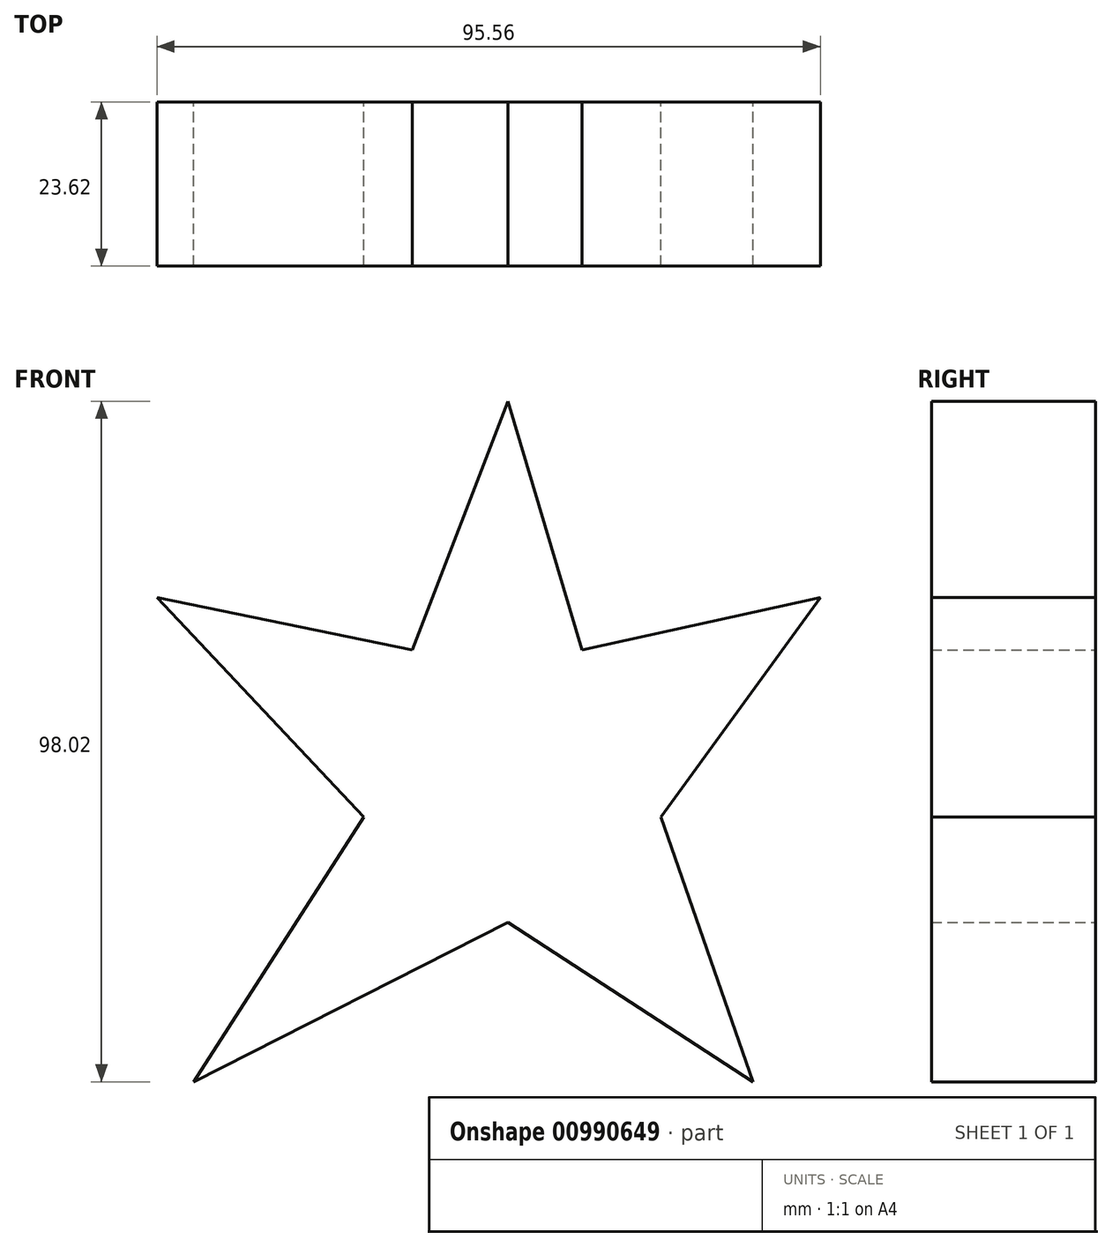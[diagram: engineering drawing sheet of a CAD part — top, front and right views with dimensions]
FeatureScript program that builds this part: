
annotation { "Feature Type Name" : "Feature", "Feature Type Description" : "" }
export const myFeature = defineFeature(function(context is Context, id is Id, definition is map)
    precondition{}
    {
        {
            var Q0;
            Q0=qCreatedBy(makeId("Front.planeOp"),FACE);
            var sketch = newSketch(context, id + "F0", { "sketchPlane" : qUnion([Q0])});
            skLineSegment(sketch, "E0", {"start": v(0, 53.18) * mm, "end": v(-13.75, 17.35) * mm});
            skLineSegment(sketch, "E1", {"start": v(-13.75, 17.35) * mm, "end": v(-50.53, 24.93) * mm});
            skLineSegment(sketch, "E2", {"start": v(-50.53, 24.93) * mm, "end": v(-20.76, -6.73) * mm});
            skLineSegment(sketch, "E3", {"start": v(-20.76, -6.73) * mm, "end": v(-45.22, -44.84) * mm});
            skLineSegment(sketch, "E4", {"start": v(-45.22, -44.84) * mm, "end": v(0, -21.9) * mm});
            skLineSegment(sketch, "E5", {"start": v(0, -21.9) * mm, "end": v(35.36, -44.84) * mm});
            skLineSegment(sketch, "E6", {"start": v(35.36, -44.84) * mm, "end": v(22.09, -6.73) * mm});
            skLineSegment(sketch, "E7", {"start": v(22.09, -6.73) * mm, "end": v(45.03, 24.93) * mm});
            skLineSegment(sketch, "E8", {"start": v(45.03, 24.93) * mm, "end": v(10.71, 17.35) * mm});
            skLineSegment(sketch, "E9", {"start": v(10.71, 17.35) * mm, "end": v(0, 53.18) * mm});
            skSolve(sketch);
        }
        {
            var Q0;
            Q0=makeQuery(id+"F0.imprint","IMPRINT",FACE,{"disambiguationData":[TD([[makeQuery(id+"F0.imprint","IMPRINT",EDGE,{"derivedFrom":sQuery(id+"F0.wireOp",EDGE,"E0")}),1.0]])]});
            extrude(context, id + "F1", {"entities" : qUnion([Q0]), "depth" : 23.62 * mm, "offsetDistance" : 25.4 * mm});
        }
    });
